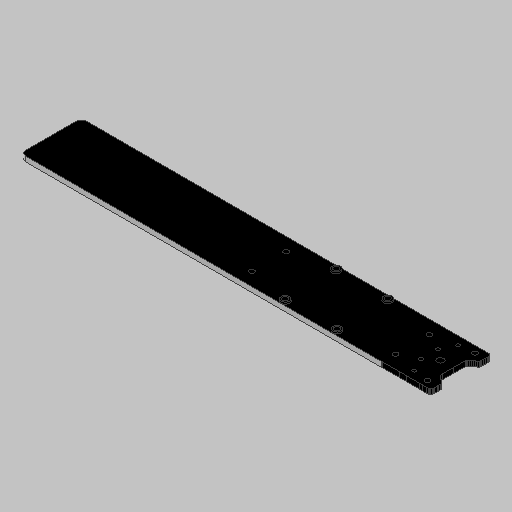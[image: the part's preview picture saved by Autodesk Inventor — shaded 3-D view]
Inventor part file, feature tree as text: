
AUTODESK INVENTOR PART (.ipt)
format: ipt  version: 2025.2 (Build 292293000, 293)  size: 2,963,456 bytes
history: native  units: in
note: dims shown in document units (in); Inventor stores cm internally (conversion verified against a paired STEP export)
features: extrude x22, sketch x22, fillet x1
ambient origin geometry x8: Origin, YZ Plane, XZ Plane, XY Plane, X Axis, Y Axis, Z Axis, Center Point
bodies: Solid1 (feature_tree)
feature tree (45):
  extrude  "Extrusion1"  Depth=0.1181in
  extrude  "Extrusion2"  Depth=0.1181in
  extrude  "Extrusion3"  Depth=0.126in
  extrude  "Extrusion4"  Depth=1.2008in
  extrude  "Extrusion5"  Depth=1.2008in
  extrude  "Extrusion6"  Depth=0.6004in
  extrude  "Extrusion7"  TaperAngle=90.0deg  [1 undecoded]
  extrude  "Extrusion8"  Depth=0.6004in
  extrude  "Extrusion9"  Depth=0.1181in TaperAngle=0.0deg
  extrude  "Extrusion10"  Depth=0.1181in
  extrude  "Extrusion11"  Depth=0.1181in TaperAngle=0.0deg
  extrude  "Extrusion12"  Depth=0.1181in
  extrude  "Extrusion13"  Depth=0.1969in
  extrude  "Extrusion14"  Depth=0.1181in TaperAngle=0.0deg
  extrude  "Extrusion15"  Depth=0.151in
  extrude  "Extrusion16"  Depth=0.1181in
  extrude  "Extrusion22"  Depth=0.1181in
  extrude  "Extrusion24"  Depth=0.1181in
  extrude  "Extrusion25"  Depth=0.3937in
  extrude  "Extrusion26"  Depth=0.3937in
  extrude  "Extrusion27"  Depth=0.1181in TaperAngle=0.0deg
  extrude  "Extrusion28"  Depth=0.1181in TaperAngle=0.0deg
  fillet  "Fillet1"  Radius=0.1181in
  sketch  "Sketch1"  dims[d0=0.1181in d1=0.0in d2=5.1217in]
  sketch  "Sketch2"  dims[d3=0.1181in d4=0.0in d5=0.126in]
  sketch  "Sketch3"  dims[d6=0.126in d7=0.126in]
  sketch  "Sketch4"  dims[d8=0.126in d9=1.2008in]
  sketch  "Sketch5"  dims[d10=1.2008in d11=1.2008in]
  sketch  "Sketch6"  dims[d12=1.2008in d13=0.6004in]
  sketch  "Sketch7"  dims[d14=0.6004in d17=90.0deg]
  sketch  "Sketch8"  dims[d18=0.6004in d19=0.6004in]
  sketch  "Sketch9"  dims[d20=0.6004in d21=0.1181in d22=0.0in]
  sketch  "Sketch10"  dims[d23=0.1181in d24=0.1181in]
  sketch  "Sketch11"  dims[d25=0.1181in d26=0.1181in d27=0.0in]
  sketch  "Sketch12"  dims[d29=0.1181in d30=0.0in d31=0.1181in]
  sketch  "Sketch13"  dims[d32=0.1969in d33=0.1969in]
  sketch  "Sketch14"  dims[d34=0.1181in d35=0.0in d36=0.1181in d37=0.0in]
  sketch  "Sketch15"  dims[d38=0.1554in d39=0.151in]
  sketch  "Sketch17"  dims[d40=0.1181in d41=0.0in d42=0.1181in]
  sketch  "Sketch23"  dims[d43=0.1181in d44=0.1181in]
  sketch  "Sketch25"  dims[d45=0.1181in d46=0.5512in]
  sketch  "Sketch26"  dims[d47=0.5512in d48=0.3937in]
  sketch  "Sketch27"  dims[d49=0.3937in d50=0.9013in]
  sketch  "Sketch28"  dims[d51=0.1181in d52=0.0in d53=0.1181in d54=0.0in]
  sketch  "Sketch29"  dims[d55=0.1575in d56=0.1181in d57=0.0in d58=0.1181in d59=0.0in d60=0.0827in d61=0.1969in d62=0.5512in d63=0.0827in d64=0.315in d65=0.1575in d66=0.1181in d67=0.0in d68=0.1969in d69=0.1969in d70=0.1969in d71=0.1969in d72=0.0394in d73=0.0in d74=0.7874in d75=0.4528in d76=1.5748in d77=0.9055in d78=0.0197in d79=0.0in d80=0.0787in d81=0.0787in d82=0.0591in d83=0.0in d100=0.0197in d101=0.0in d114=0.1181in d115=0.0in d116=0.1181in d117=0.0in d118=0.1181in d119=0.0in d120=0.3937in d121=0.0in d122=0.1181in d123=0.0in d124=0.1181in d90=0.0197in d91=0.0344in d92=0.0197in d93=0.0344in]
note: 1 required parameter value undecoded (feature->parameter linkage not recoverable at this tier; creation-order binding heuristic only, values carry confidence <= 0.55)
